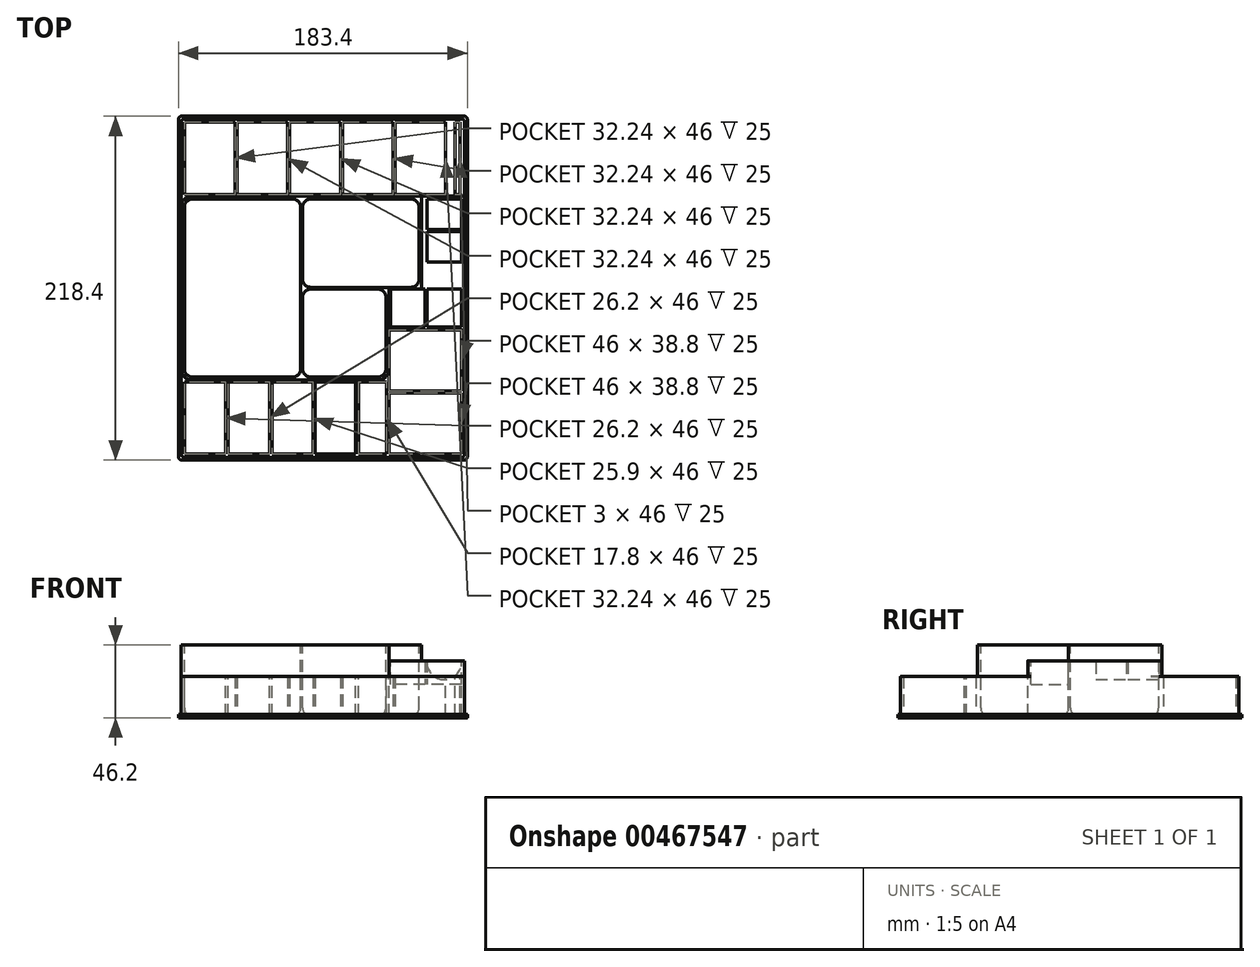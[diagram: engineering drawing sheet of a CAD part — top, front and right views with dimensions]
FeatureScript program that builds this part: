
annotation { "Feature Type Name" : "Feature", "Feature Type Description" : "" }
export const myFeature = defineFeature(function(context is Context, id is Id, definition is map)
    precondition{}
    {
        {
            var Q0;
            Q0=qCreatedBy(makeId("Top.planeOp"),FACE);
            var sketch = newSketch(context, id + "F0", { "sketchPlane" : qUnion([Q0])});
            skLineSegment(sketch, "E0.bottom", {"start": v(0, 0) * mm, "end": v(180, 0) * mm});
            skLineSegment(sketch, "E0.top", {"start": v(0, 215) * mm, "end": v(180, 215) * mm});
            skLineSegment(sketch, "E0.left", {"start": v(0, 0) * mm, "end": v(0, 215) * mm});
            skLineSegment(sketch, "E0.right", {"start": v(180, 0) * mm, "end": v(180, 215) * mm});
            skSolve(sketch);
        }
        {
            var Q0;
            Q0=qSketchRegion(id+"F0",true);
            extrude(context, id + "F1", {"entities" : qUnion([Q0]), "depth" : 25 * mm});
        }
        {
            var Q0;
            Q0=makeQuery(id+"F1.opExtrude","CAP_FACE",FACE,{"disambiguationData":[OSD([sQuery(id+"F0.wireOp",EDGE,"E0.bottom"),sQuery(id+"F0.wireOp",EDGE,"E0.top"),sQuery(id+"F0.wireOp",EDGE,"E0.left"),sQuery(id+"F0.wireOp",EDGE,"E0.right")])],"isStart":false});
            var sketch = newSketch(context, id + "F2", { "sketchPlane" : qUnion([Q0])});
            skLineSegment(sketch, "E1.bottom", {"start": v(2, 167) * mm, "end": v(2, 213) * mm});
            skLineSegment(sketch, "E1.top", {"start": v(168, 167) * mm, "end": v(168, 213) * mm});
            skLineSegment(sketch, "E1.left", {"start": v(2, 167) * mm, "end": v(168, 167) * mm});
            skLineSegment(sketch, "E1.right", {"start": v(2, 213) * mm, "end": v(168, 213) * mm});
            skLineSegment(sketch, "E2.bottom", {"start": v(110.8, 48) * mm, "end": v(57.8, 48) * mm});
            skLineSegment(sketch, "E2.top", {"start": v(110.8, 2) * mm, "end": v(57.8, 2) * mm});
            skLineSegment(sketch, "E2.left", {"start": v(110.8, 48) * mm, "end": v(110.8, 2) * mm});
            skLineSegment(sketch, "E2.right", {"start": v(57.8, 48) * mm, "end": v(57.8, 2) * mm});
            skLineSegment(sketch, "E3.bottom", {"start": v(2, 2) * mm, "end": v(28.2, 2) * mm});
            skLineSegment(sketch, "E3.top", {"start": v(2, 48) * mm, "end": v(28.2, 48) * mm});
            skLineSegment(sketch, "E3.left", {"start": v(2, 2) * mm, "end": v(2, 48) * mm});
            skLineSegment(sketch, "E3.right", {"start": v(28.2, 2) * mm, "end": v(28.2, 48) * mm});
            skLineSegment(sketch, "E4.bottom", {"start": v(132, 40.8) * mm, "end": v(178, 40.8) * mm});
            skLineSegment(sketch, "E4.top", {"start": v(132, 2) * mm, "end": v(178, 2) * mm});
            skLineSegment(sketch, "E4.left", {"start": v(132, 40.8) * mm, "end": v(132, 2) * mm});
            skLineSegment(sketch, "E4.right", {"start": v(178, 40.8) * mm, "end": v(178, 2) * mm});
            skLineSegment(sketch, "E5.bottom", {"start": v(132, 42) * mm, "end": v(178, 42) * mm});
            skLineSegment(sketch, "E5.top", {"start": v(132, 80.8) * mm, "end": v(178, 80.8) * mm});
            skLineSegment(sketch, "E5.left", {"start": v(132, 42) * mm, "end": v(132, 80.8) * mm});
            skLineSegment(sketch, "E5.right", {"start": v(178, 42) * mm, "end": v(178, 80.8) * mm});
            skLineSegment(sketch, "E6.bottom", {"start": v(29.9, 48) * mm, "end": v(56.1, 48) * mm});
            skLineSegment(sketch, "E6.top", {"start": v(29.9, 2) * mm, "end": v(56.1, 2) * mm});
            skLineSegment(sketch, "E6.left", {"start": v(29.9, 48) * mm, "end": v(29.9, 2) * mm});
            skLineSegment(sketch, "E6.right", {"start": v(56.1, 48) * mm, "end": v(56.1, 2) * mm});
            skLineSegment(sketch, "E7.bottom", {"start": v(130, 51) * mm, "end": v(77.1, 51) * mm});
            skLineSegment(sketch, "E7.top", {"start": v(130, 106.8) * mm, "end": v(77.1, 106.8) * mm});
            skLineSegment(sketch, "E7.right", {"start": v(77.1, 51) * mm, "end": v(77.1, 106.8) * mm});
            skLineSegment(sketch, "E8.top", {"start": v(178, 82.8) * mm, "end": v(178, 106.8) * mm});
            skLineSegment(sketch, "E8.left", {"start": v(133, 82.8) * mm, "end": v(178, 82.8) * mm});
            skLineSegment(sketch, "E8.right", {"start": v(133, 106.8) * mm, "end": v(178, 106.8) * mm});
            skLineSegment(sketch, "E9", {"start": v(2, 25) * mm, "end": v(0, 25) * mm, "construction": true});
            skLineSegment(sketch, "E10", {"start": v(28.2, 25) * mm, "end": v(29.9, 25) * mm, "construction": true});
            skLineSegment(sketch, "E11.bottom", {"start": v(156, 164) * mm, "end": v(178, 164) * mm});
            skLineSegment(sketch, "E11.top", {"start": v(156, 124) * mm, "end": v(178, 124) * mm});
            skLineSegment(sketch, "E11.left", {"start": v(156, 164) * mm, "end": v(156, 124) * mm});
            skLineSegment(sketch, "E11.right", {"start": v(178, 164) * mm, "end": v(178, 124) * mm});
            skLineSegment(sketch, "E12.bottom", {"start": v(151, 108) * mm, "end": v(77.1, 108) * mm});
            skLineSegment(sketch, "E12.top", {"start": v(151, 164) * mm, "end": v(77.1, 164) * mm});
            skLineSegment(sketch, "E12.left", {"start": v(151, 108) * mm, "end": v(151, 164) * mm});
            skLineSegment(sketch, "E12.right", {"start": v(77.1, 108) * mm, "end": v(77.1, 164) * mm});
            skLineSegment(sketch, "E13.bottom", {"start": v(2, 51) * mm, "end": v(75.9, 51) * mm});
            skLineSegment(sketch, "E13.top", {"start": v(2, 164) * mm, "end": v(75.9, 164) * mm});
            skLineSegment(sketch, "E13.left", {"start": v(2, 51) * mm, "end": v(2, 164) * mm});
            skLineSegment(sketch, "E13.right", {"start": v(75.9, 51) * mm, "end": v(75.9, 164) * mm});
            skLineSegment(sketch, "E14", {"start": v(133, 82.8) * mm, "end": v(133, 106.8) * mm});
            skLineSegment(sketch, "E15.bottom", {"start": v(130.3, 48) * mm, "end": v(130.3, 2) * mm});
            skLineSegment(sketch, "E15.top", {"start": v(112.5, 48) * mm, "end": v(112.5, 2) * mm});
            skLineSegment(sketch, "E15.left", {"start": v(130.3, 48) * mm, "end": v(112.5, 48) * mm});
            skLineSegment(sketch, "E15.right", {"start": v(130.3, 2) * mm, "end": v(112.5, 2) * mm});
            skLineSegment(sketch, "E16.bottom", {"start": v(174, 213) * mm, "end": v(177, 213) * mm});
            skLineSegment(sketch, "E16.top", {"start": v(174, 167) * mm, "end": v(177, 167) * mm});
            skLineSegment(sketch, "E16.left", {"start": v(174, 213) * mm, "end": v(174, 167) * mm});
            skLineSegment(sketch, "E16.right", {"start": v(177, 213) * mm, "end": v(177, 167) * mm});
            skLineSegment(sketch, "E17", {"start": v(56.1, 25) * mm, "end": v(57.8, 25) * mm, "construction": true});
            skLineSegment(sketch, "E18", {"start": v(110.8, 25) * mm, "end": v(112.5, 25) * mm, "construction": true});
            skLineSegment(sketch, "E19", {"start": v(130.3, 25) * mm, "end": v(132, 25) * mm, "construction": true});
            skLineSegment(sketch, "E20", {"start": v(130, 51) * mm, "end": v(130, 106.8) * mm});
            skSolve(sketch);
        }
        {
            var Q0;
            Q0=qSketchRegion(id+"F2",true);
            extrude(context, id + "F3", {"entities" : qUnion([Q0]), "operationType" : NewBodyOperationType.REMOVE, "endBound" : BoundingType.THROUGH_ALL, "oppositeDirection" : true, "depth" : 25 * mm});
        }
        {
            var Q0;
            Q0=qCreatedBy(makeId("Top.planeOp"),FACE);
            var sketch = newSketch(context, id + "F4", { "sketchPlane" : qUnion([Q0])});
            skLineSegment(sketch, "E21.0", {"start": v(0, 215) * mm, "end": v(180, 215) * mm});
            skLineSegment(sketch, "E21.1", {"start": v(0, 0) * mm, "end": v(0, 215) * mm});
            skLineSegment(sketch, "E21.2", {"start": v(0, 0) * mm, "end": v(180, 0) * mm});
            skLineSegment(sketch, "E21.3", {"start": v(180, 0) * mm, "end": v(180, 215) * mm});
            skSolve(sketch);
        }
        {
            var Q0;
            Q0=qSketchRegion(id+"F4",true);
            extrude(context, id + "F5", {"entities" : qUnion([Q0]), "operationType" : NewBodyOperationType.ADD, "oppositeDirection" : true, "depth" : 1.2 * mm});
        }
        {
            var Q0;
            Q0=qCreatedBy(makeId("Top.planeOp"),FACE);
            var sketch = newSketch(context, id + "F6", { "sketchPlane" : qUnion([Q0])});
            skLineSegment(sketch, "E22.bottom", {"start": v(34.24, 167) * mm, "end": v(34.24, 213) * mm});
            skLineSegment(sketch, "E22.top", {"start": v(35.44, 167) * mm, "end": v(35.44, 213) * mm});
            skLineSegment(sketch, "E22.left", {"start": v(34.24, 167) * mm, "end": v(35.44, 167) * mm});
            skLineSegment(sketch, "E22.right", {"start": v(34.24, 213) * mm, "end": v(35.44, 213) * mm});
            skLineSegment(sketch, "E23.0.1.0", {"start": v(67.68, 167) * mm, "end": v(67.68, 213) * mm});
            skLineSegment(sketch, "E23.0.1.1", {"start": v(68.88, 167) * mm, "end": v(68.88, 213) * mm});
            skLineSegment(sketch, "E23.0.1.2", {"start": v(67.68, 167) * mm, "end": v(68.88, 167) * mm});
            skLineSegment(sketch, "E23.0.1.3", {"start": v(67.68, 213) * mm, "end": v(68.88, 213) * mm});
            skLineSegment(sketch, "E23.0.2.0", {"start": v(101.12, 167) * mm, "end": v(101.12, 213) * mm});
            skLineSegment(sketch, "E23.0.2.1", {"start": v(102.32, 167) * mm, "end": v(102.32, 213) * mm});
            skLineSegment(sketch, "E23.0.2.2", {"start": v(101.12, 167) * mm, "end": v(102.32, 167) * mm});
            skLineSegment(sketch, "E23.0.2.3", {"start": v(101.12, 213) * mm, "end": v(102.32, 213) * mm});
            skLineSegment(sketch, "E23.direction1", {"start": v(35.44, 167) * mm, "end": v(35.44, 200.98) * mm, "construction": true});
            skLineSegment(sketch, "E23.direction2", {"start": v(35.44, 167) * mm, "end": v(68.88, 167) * mm, "construction": true});
            skLineSegment(sketch, "E24.0.0.3", {"start": v(134.56, 167) * mm, "end": v(134.56, 213) * mm});
            skLineSegment(sketch, "E24.3.0.3", {"start": v(135.76, 167) * mm, "end": v(135.76, 213) * mm});
            skLineSegment(sketch, "E24.6.0.3", {"start": v(134.56, 167) * mm, "end": v(135.76, 167) * mm});
            skLineSegment(sketch, "E24.9.0.3", {"start": v(134.56, 213) * mm, "end": v(135.76, 213) * mm});
            skLineSegment(sketch, "E25", {"start": v(34.24, 190) * mm, "end": v(2, 190) * mm, "construction": true});
            skPoint(sketch, "E25.endSnap0", {"position": v(34.24, 190) * mm});
            skLineSegment(sketch, "E26", {"start": v(135.76, 190) * mm, "end": v(168, 190) * mm, "construction": true});
            skLineSegment(sketch, "E27", {"start": v(35.44, 190) * mm, "end": v(67.68, 190) * mm, "construction": true});
            skLineSegment(sketch, "E28.bottom", {"start": v(83.7, 48) * mm, "end": v(84.9, 48) * mm});
            skLineSegment(sketch, "E28.top", {"start": v(83.7, 2) * mm, "end": v(84.9, 2) * mm});
            skLineSegment(sketch, "E28.left", {"start": v(83.7, 48) * mm, "end": v(83.7, 2) * mm});
            skLineSegment(sketch, "E28.right", {"start": v(84.9, 48) * mm, "end": v(84.9, 2) * mm});
            skLineSegment(sketch, "E29", {"start": v(83.7, 25) * mm, "end": v(57.8, 25) * mm, "construction": true});
            skLineSegment(sketch, "E30", {"start": v(84.9, 25) * mm, "end": v(110.8, 25) * mm, "construction": true});
            skLineSegment(sketch, "E31.bottom", {"start": v(156, 144.6) * mm, "end": v(178, 144.6) * mm});
            skLineSegment(sketch, "E31.top", {"start": v(156, 143.4) * mm, "end": v(178, 143.4) * mm});
            skLineSegment(sketch, "E31.left", {"start": v(156, 144.6) * mm, "end": v(156, 143.4) * mm});
            skLineSegment(sketch, "E31.right", {"start": v(178, 144.6) * mm, "end": v(178, 143.4) * mm});
            skLineSegment(sketch, "E32.bottom", {"start": v(156.1, 82.8) * mm, "end": v(156.1, 106.8) * mm});
            skLineSegment(sketch, "E32.top", {"start": v(154.9, 82.8) * mm, "end": v(154.9, 106.8) * mm});
            skLineSegment(sketch, "E32.left", {"start": v(154.9, 82.8) * mm, "end": v(156.1, 82.8) * mm});
            skLineSegment(sketch, "E32.right", {"start": v(154.9, 106.8) * mm, "end": v(156.1, 106.8) * mm});
            skSolve(sketch);
        }
        {
            var Q0;
            Q0=qSketchRegion(id+"F6",true);
            var Q1;
            Q1=makeQuery(id+"F1.opExtrude","CAP_FACE",FACE,{"disambiguationData":[OSD([sQuery(id+"F0.wireOp",EDGE,"E0.bottom"),sQuery(id+"F0.wireOp",EDGE,"E0.top"),sQuery(id+"F0.wireOp",EDGE,"E0.left"),sQuery(id+"F0.wireOp",EDGE,"E0.right")])],"isStart":false});
            extrude(context, id + "F7", {"entities" : qUnion([Q0]), "operationType" : NewBodyOperationType.ADD, "endBound" : BoundingType.UP_TO_SURFACE, "endBoundEntityFace" : qUnion([Q1]), "depth" : 25 * mm});
        }
        {
            var Q0;
            {var subQ0=sQuery(id+"F0.wireOp",EDGE,"E0.right");var subQ1=sQuery(id+"F0.wireOp",EDGE,"E0.left");var subQ2=sQuery(id+"F0.wireOp",EDGE,"E0.top");var subQ3=sQuery(id+"F0.wireOp",EDGE,"E0.bottom");Q0=makeQuery(id+"F7.boolean.opBoolean","MERGE",FACE,{"derivedFrom":[makeQuery(id+"F1.opExtrude","CAP_FACE",FACE,{"disambiguationData":[OSD([subQ3,subQ2,subQ1,subQ0])],"isStart":false}),makeQuery(id+"F7.opExtrude","CAP_FACE",FACE,{"disambiguationData":[OSD([subQ3,subQ2,subQ1,subQ0]),ownerDisambiguation([makeQuery(id+"F6.imprint","IMPRINT",EDGE,{"derivedFrom":sQuery(id+"F6.wireOp",EDGE,"E22.bottom")})])],"isStart":false}),makeQuery(id+"F7.opExtrude","CAP_FACE",FACE,{"disambiguationData":[OSD([subQ3,subQ2,subQ1,subQ0]),ownerDisambiguation([makeQuery(id+"F6.imprint","IMPRINT",EDGE,{"derivedFrom":sQuery(id+"F6.wireOp",EDGE,"E23.0.1.0")})])],"isStart":false}),makeQuery(id+"F7.opExtrude","CAP_FACE",FACE,{"disambiguationData":[OSD([subQ3,subQ2,subQ1,subQ0]),ownerDisambiguation([makeQuery(id+"F6.imprint","IMPRINT",EDGE,{"derivedFrom":sQuery(id+"F6.wireOp",EDGE,"E23.0.2.0")})])],"isStart":false}),makeQuery(id+"F7.opExtrude","CAP_FACE",FACE,{"disambiguationData":[OSD([subQ3,subQ2,subQ1,subQ0]),ownerDisambiguation([makeQuery(id+"F6.imprint","IMPRINT",EDGE,{"derivedFrom":sQuery(id+"F6.wireOp",EDGE,"E24.0.0.3")})])],"isStart":false}),makeQuery(id+"F7.opExtrude","CAP_FACE",FACE,{"disambiguationData":[OSD([subQ3,subQ2,subQ1,subQ0]),ownerDisambiguation([makeQuery(id+"F6.imprint","IMPRINT",EDGE,{"derivedFrom":sQuery(id+"F6.wireOp",EDGE,"E28.bottom")})])],"isStart":false}),makeQuery(id+"F7.opExtrude","CAP_FACE",FACE,{"disambiguationData":[OSD([subQ3,subQ2,subQ1,subQ0]),ownerDisambiguation([makeQuery(id+"F6.imprint","IMPRINT",EDGE,{"derivedFrom":sQuery(id+"F6.wireOp",EDGE,"E31.bottom")})])],"isStart":false}),makeQuery(id+"F7.opExtrude","CAP_FACE",FACE,{"disambiguationData":[OSD([subQ3,subQ2,subQ1,subQ0]),ownerDisambiguation([makeQuery(id+"F6.imprint","IMPRINT",EDGE,{"derivedFrom":sQuery(id+"F6.wireOp",EDGE,"E32.bottom")})])],"isStart":false})]});}
            var sketch = newSketch(context, id + "F8", { "sketchPlane" : qUnion([Q0])});
            skLineSegment(sketch, "E33.0", {"start": v(156.1, 82.8) * mm, "end": v(178, 82.8) * mm});
            skLineSegment(sketch, "E34.0", {"start": v(156.1, 82.8) * mm, "end": v(156.1, 106.8) * mm});
            skLineSegment(sketch, "E35.0", {"start": v(156.1, 106.8) * mm, "end": v(178, 106.8) * mm});
            skLineSegment(sketch, "E36.0", {"start": v(178, 82.8) * mm, "end": v(178, 106.8) * mm});
            skLineSegment(sketch, "E36.1", {"start": v(154.9, 82.8) * mm, "end": v(154.9, 106.8) * mm});
            skLineSegment(sketch, "E36.2", {"start": v(133, 82.8) * mm, "end": v(154.9, 82.8) * mm});
            skLineSegment(sketch, "E36.3", {"start": v(133, 82.8) * mm, "end": v(133, 106.8) * mm});
            skLineSegment(sketch, "E36.4", {"start": v(133, 106.8) * mm, "end": v(154.9, 106.8) * mm});
            skLineSegment(sketch, "E37.0", {"start": v(156, 124) * mm, "end": v(178, 124) * mm});
            skLineSegment(sketch, "E37.1", {"start": v(156, 143.4) * mm, "end": v(156, 124) * mm});
            skLineSegment(sketch, "E37.2", {"start": v(156, 143.4) * mm, "end": v(178, 143.4) * mm});
            skLineSegment(sketch, "E37.3", {"start": v(178, 143.4) * mm, "end": v(178, 124) * mm});
            skLineSegment(sketch, "E37.4", {"start": v(178, 164) * mm, "end": v(178, 144.6) * mm});
            skLineSegment(sketch, "E37.5", {"start": v(156, 144.6) * mm, "end": v(178, 144.6) * mm});
            skLineSegment(sketch, "E37.6", {"start": v(156, 164) * mm, "end": v(156, 144.6) * mm});
            skLineSegment(sketch, "E37.7", {"start": v(156, 164) * mm, "end": v(178, 164) * mm});
            skLineSegment(sketch, "E38.0", {"start": v(2, 51) * mm, "end": v(75.9, 51) * mm});
            skLineSegment(sketch, "E38.1", {"start": v(2, 51) * mm, "end": v(2, 164) * mm});
            skLineSegment(sketch, "E38.2", {"start": v(2, 164) * mm, "end": v(75.9, 164) * mm});
            skLineSegment(sketch, "E38.3", {"start": v(75.9, 51) * mm, "end": v(75.9, 164) * mm});
            skLineSegment(sketch, "E39.0", {"start": v(130, 51) * mm, "end": v(77.1, 51) * mm});
            skLineSegment(sketch, "E39.1", {"start": v(77.1, 51) * mm, "end": v(77.1, 106.8) * mm});
            skLineSegment(sketch, "E39.2", {"start": v(151, 108) * mm, "end": v(77.1, 108) * mm});
            skLineSegment(sketch, "E39.3", {"start": v(130, 106.8) * mm, "end": v(77.1, 106.8) * mm});
            skLineSegment(sketch, "E39.4", {"start": v(77.1, 108) * mm, "end": v(77.1, 164) * mm});
            skLineSegment(sketch, "E39.7", {"start": v(151, 164) * mm, "end": v(77.1, 164) * mm});
            skLineSegment(sketch, "E40.0", {"start": v(151, 108) * mm, "end": v(151, 164) * mm});
            skLineSegment(sketch, "E40.1", {"start": v(130, 51) * mm, "end": v(130, 106.8) * mm});
            skLineSegment(sketch, "E41", {"start": v(0, 49) * mm, "end": v(132, 49) * mm});
            skLineSegment(sketch, "E42", {"start": v(132, 49) * mm, "end": v(132, 80.8) * mm});
            skLineSegment(sketch, "E43", {"start": v(132, 80.8) * mm, "end": v(180, 80.8) * mm});
            skLineSegment(sketch, "E44", {"start": v(180, 80.8) * mm, "end": v(180, 166) * mm});
            skLineSegment(sketch, "E45", {"start": v(180, 166) * mm, "end": v(132, 166) * mm});
            skLineSegment(sketch, "E46", {"start": v(132, 166) * mm, "end": v(132, 166) * mm});
            skLineSegment(sketch, "E47", {"start": v(132, 166) * mm, "end": v(0, 166) * mm});
            skLineSegment(sketch, "E48", {"start": v(0, 166) * mm, "end": v(0, 49) * mm});
            skLineSegment(sketch, "E49", {"start": v(2, 51) * mm, "end": v(2, 49) * mm, "construction": true});
            skLineSegment(sketch, "E50", {"start": v(2, 164) * mm, "end": v(2, 166) * mm, "construction": true});
            skLineSegment(sketch, "E51", {"start": v(130, 51) * mm, "end": v(132, 51) * mm, "construction": true});
            skLineSegment(sketch, "E52", {"start": v(130, 51) * mm, "end": v(130, 49) * mm, "construction": true});
            skLineSegment(sketch, "E53", {"start": v(167, 164) * mm, "end": v(167, 166) * mm, "construction": true});
            skLineSegment(sketch, "E54", {"start": v(2, 51) * mm, "end": v(0, 51) * mm, "construction": true});
            skSolve(sketch);
        }
        {
            var Q0;
            Q0 = qSketchRegion(id + "F8", true);
            extrude(context, id + "F9", {"entities" : qUnion([Q0]), "operationType" : NewBodyOperationType.ADD, "depth" : 20 * mm});
        }
        {
            var Q0;
            Q0=makeQuery(id+"F3.boolean.opBoolean","COPY",FACE,{"derivedFrom":makeQuery(id+"F3.opExtrude","SWEPT_FACE",FACE,{"disambiguationData":[OSD([sQuery(id+"F2.wireOp",EDGE,"E14")])]})});
            var sketch = newSketch(context, id + "F10", { "sketchPlane" : qUnion([Q0])});
            skLineSegment(sketch, "E55.0", {"start": v(106.8, 0) * mm, "end": v(106.8, 20) * mm});
            skLineSegment(sketch, "E55.1", {"start": v(82.8, 0) * mm, "end": v(82.8, 20) * mm});
            skLineSegment(sketch, "E55.2", {"start": v(82.8, 0) * mm, "end": v(106.8, 0) * mm});
            skLineSegment(sketch, "E56", {"start": v(82.8, 20) * mm, "end": v(106.8, 20) * mm});
            skSolve(sketch);
        }
        {
            var Q0;
            Q0=qSketchRegion(id+"F10",true);
            var Q1;
            Q1=makeQuery(id+"F3.boolean.opBoolean","COPY",FACE,{"derivedFrom":makeQuery(id+"F3.opExtrude","SWEPT_FACE",FACE,{"disambiguationData":[OSD([sQuery(id+"F2.wireOp",EDGE,"E8.top")])]})});
            extrude(context, id + "F11", {"entities" : qUnion([Q0]), "operationType" : NewBodyOperationType.ADD, "endBound" : BoundingType.UP_TO_SURFACE, "endBoundEntityFace" : qUnion([Q1]), "depth" : 25 * mm});
        }
        {
            var Q0;
            Q0=makeQuery(id+"F3.boolean.opBoolean","COPY",FACE,{"derivedFrom":makeQuery(id+"F3.opExtrude","SWEPT_FACE",FACE,{"disambiguationData":[OSD([sQuery(id+"F2.wireOp",EDGE,"E11.bottom")])]})});
            var sketch = newSketch(context, id + "F12", { "sketchPlane" : qUnion([Q0])});
            skLineSegment(sketch, "E57.0", {"start": v(156, 0) * mm, "end": v(156, 34) * mm});
            skLineSegment(sketch, "E57.1", {"start": v(178, 0) * mm, "end": v(178, 34) * mm});
            skLineSegment(sketch, "E57.2", {"start": v(156, 0) * mm, "end": v(178, 0) * mm});
            skArc(sketch, "E58", {"start": v(156, 34) * mm, "mid": v(167, 23) * mm, "end": v(178, 34) * mm});
            skSolve(sketch);
        }
        {
            var Q0;
            Q0=qSketchRegion(id+"F12",true);
            var Q1;
            Q1=makeQuery(id+"F3.boolean.opBoolean","COPY",FACE,{"derivedFrom":makeQuery(id+"F3.opExtrude","SWEPT_FACE",FACE,{"disambiguationData":[OSD([sQuery(id+"F2.wireOp",EDGE,"E11.top")])]})});
            extrude(context, id + "F13", {"entities" : qUnion([Q0]), "operationType" : NewBodyOperationType.ADD, "endBound" : BoundingType.UP_TO_SURFACE, "endBoundEntityFace" : qUnion([Q1]), "depth" : 25 * mm});
        }
        {
            var Q0;
            Q0=makeQuery(id+"F5.opExtrude","CAP_FACE",FACE,{"disambiguationData":[OSD([sQuery(id+"F4.wireOp",EDGE,"E21.0"),sQuery(id+"F4.wireOp",EDGE,"E21.1"),sQuery(id+"F4.wireOp",EDGE,"E21.2"),sQuery(id+"F4.wireOp",EDGE,"E21.3")])],"isStart":false});
            var sketch = newSketch(context, id + "F14", { "sketchPlane" : qUnion([Q0])});
            skLineSegment(sketch, "E59", {"start": v(0, 0) * mm, "end": v(180, 0) * mm});
            skLineSegment(sketch, "E60", {"start": v(0, 0) * mm, "end": v(0, -215) * mm});
            skLineSegment(sketch, "E61", {"start": v(0, -215) * mm, "end": v(180, -215) * mm});
            skLineSegment(sketch, "E62", {"start": v(180, 0) * mm, "end": v(180, -215) * mm});
            skLineSegment(sketch, "E63.0", {"start": v(181.7, 1.7) * mm, "end": v(181.7, -216.7) * mm});
            skLineSegment(sketch, "E63.1", {"start": v(-1.7, 1.7) * mm, "end": v(181.7, 1.7) * mm});
            skLineSegment(sketch, "E63.2", {"start": v(-1.7, 1.7) * mm, "end": v(-1.7, -216.7) * mm});
            skLineSegment(sketch, "E63.3", {"start": v(-1.7, -216.7) * mm, "end": v(181.7, -216.7) * mm});
            skSolve(sketch);
        }
        {
            var Q0;
            Q0=qSketchRegion(id+"F14",true);
            extrude(context, id + "F15", {"entities" : qUnion([Q0]), "operationType" : NewBodyOperationType.ADD, "oppositeDirection" : true, "depth" : 2 * mm});
        }
        {
            var Q0;
            Q0=makeQuery(id+"F9.opExtrude","CAP_FACE",FACE,{"disambiguationData":[OSD([sQuery(id+"F8.wireOp",EDGE,"E33.0"),sQuery(id+"F8.wireOp",EDGE,"E34.0"),sQuery(id+"F8.wireOp",EDGE,"E35.0"),sQuery(id+"F8.wireOp",EDGE,"E36.0"),sQuery(id+"F8.wireOp",EDGE,"E36.1"),sQuery(id+"F8.wireOp",EDGE,"E36.2"),sQuery(id+"F8.wireOp",EDGE,"E36.3"),sQuery(id+"F8.wireOp",EDGE,"E36.4"),sQuery(id+"F8.wireOp",EDGE,"E37.0"),sQuery(id+"F8.wireOp",EDGE,"E37.1"),sQuery(id+"F8.wireOp",EDGE,"E37.2"),sQuery(id+"F8.wireOp",EDGE,"E37.3"),sQuery(id+"F8.wireOp",EDGE,"E37.4"),sQuery(id+"F8.wireOp",EDGE,"E37.5"),sQuery(id+"F8.wireOp",EDGE,"E37.6"),sQuery(id+"F8.wireOp",EDGE,"E37.7"),sQuery(id+"F8.wireOp",EDGE,"E38.0"),sQuery(id+"F8.wireOp",EDGE,"E38.1"),sQuery(id+"F8.wireOp",EDGE,"E38.2"),sQuery(id+"F8.wireOp",EDGE,"E38.3"),sQuery(id+"F8.wireOp",EDGE,"E39.0"),sQuery(id+"F8.wireOp",EDGE,"E39.1"),sQuery(id+"F8.wireOp",EDGE,"E39.2"),sQuery(id+"F8.wireOp",EDGE,"E39.3"),sQuery(id+"F8.wireOp",EDGE,"E39.4"),sQuery(id+"F8.wireOp",EDGE,"E39.5"),sQuery(id+"F8.wireOp",EDGE,"E39.6"),sQuery(id+"F8.wireOp",EDGE,"E39.7"),sQuery(id+"F8.wireOp",EDGE,"E40.0"),sQuery(id+"F8.wireOp",EDGE,"E40.1"),sQuery(id+"F8.wireOp",EDGE,"E41"),sQuery(id+"F8.wireOp",EDGE,"XPu77cuN-X5yf-Tfu9-wkux-P44unaFSe9BC"),sQuery(id+"F8.wireOp",EDGE,"gCxIZk9a-GLua-Ydf3-ZZly-w7nDAVDTeZa5"),sQuery(id+"F8.wireOp",EDGE,"E42"),sQuery(id+"F8.wireOp",EDGE,"E43"),sQuery(id+"F8.wireOp",EDGE,"E44"),sQuery(id+"F8.wireOp",EDGE,"E45"),sQuery(id+"F8.wireOp",EDGE,"E46"),sQuery(id+"F8.wireOp",EDGE,"E47"),sQuery(id+"F8.wireOp",EDGE,"E48")])],"isStart":false});
            var sketch = newSketch(context, id + "F16", { "sketchPlane" : qUnion([Q0])});
            skLineSegment(sketch, "E64.0", {"start": v(132, 80.8) * mm, "end": v(180, 80.8) * mm});
            skLineSegment(sketch, "E64.1", {"start": v(180, 80.8) * mm, "end": v(180, 166) * mm});
            skLineSegment(sketch, "E64.2", {"start": v(180, 166) * mm, "end": v(152.5, 166) * mm});
            skLineSegment(sketch, "E65", {"start": v(132, 80.8) * mm, "end": v(132, 106.8) * mm});
            skLineSegment(sketch, "E66", {"start": v(132, 106.8) * mm, "end": v(152.5, 106.8) * mm});
            skLineSegment(sketch, "E67", {"start": v(152.5, 106.8) * mm, "end": v(152.5, 166) * mm});
            skSolve(sketch);
        }
        {
            var Q0;
            Q0 = qSketchRegion(id + "F16", true);
            extrude(context, id + "F17", {"entities" : qUnion([Q0]), "operationType" : NewBodyOperationType.REMOVE, "oppositeDirection" : true, "depth" : 10 * mm});
        }
        {
            var Q0;
            Q0=makeQuery(id+"F5.boolean.opBoolean","MERGE",EDGE,{"derivedFrom":[makeQuery(id+"F1.opExtrude","SWEPT_EDGE",EDGE,{"disambiguationData":[OSD([sQuery(id+"F0.wireOp",EDGE,"E0.bottom"),sQuery(id+"F0.wireOp",EDGE,"E0.right")])]}),makeQuery(id+"F5.opExtrude","SWEPT_EDGE",EDGE,{"disambiguationData":[OSD([sQuery(id+"F4.wireOp",EDGE,"E21.2"),sQuery(id+"F4.wireOp",EDGE,"E21.3")])]})]});
            var Q1;
            Q1=makeQuery(id+"F9.opExtrude","SWEPT_EDGE",EDGE,{"disambiguationData":[OSD([sQuery(id+"F0.wireOp",EDGE,"E0.right"),sQuery(id+"F8.wireOp",EDGE,"E43"),sQuery(id+"F8.wireOp",EDGE,"E44")])]});
            var Q2;
            Q2=makeQuery(id+"F9.opExtrude","SWEPT_EDGE",EDGE,{"disambiguationData":[OSD([sQuery(id+"F0.wireOp",EDGE,"E0.right"),sQuery(id+"F8.wireOp",EDGE,"E44"),sQuery(id+"F8.wireOp",EDGE,"E45")])]});
            var Q3;
            Q3=makeQuery(id+"F5.boolean.opBoolean","MERGE",EDGE,{"derivedFrom":[makeQuery(id+"F1.opExtrude","SWEPT_EDGE",EDGE,{"disambiguationData":[OSD([sQuery(id+"F0.wireOp",EDGE,"E0.top"),sQuery(id+"F0.wireOp",EDGE,"E0.right")])]}),makeQuery(id+"F5.opExtrude","SWEPT_EDGE",EDGE,{"disambiguationData":[OSD([sQuery(id+"F4.wireOp",EDGE,"E21.0"),sQuery(id+"F4.wireOp",EDGE,"E21.3")])]})]});
            var Q4;
            Q4=makeQuery(id+"F5.boolean.opBoolean","MERGE",EDGE,{"derivedFrom":[makeQuery(id+"F1.opExtrude","SWEPT_EDGE",EDGE,{"disambiguationData":[OSD([sQuery(id+"F0.wireOp",EDGE,"E0.top"),sQuery(id+"F0.wireOp",EDGE,"E0.left")])]}),makeQuery(id+"F5.opExtrude","SWEPT_EDGE",EDGE,{"disambiguationData":[OSD([sQuery(id+"F4.wireOp",EDGE,"E21.0"),sQuery(id+"F4.wireOp",EDGE,"E21.1")])]})]});
            var Q5;
            Q5=makeQuery(id+"F5.boolean.opBoolean","MERGE",EDGE,{"derivedFrom":[makeQuery(id+"F1.opExtrude","SWEPT_EDGE",EDGE,{"disambiguationData":[OSD([sQuery(id+"F0.wireOp",EDGE,"E0.bottom"),sQuery(id+"F0.wireOp",EDGE,"E0.left")])]}),makeQuery(id+"F5.opExtrude","SWEPT_EDGE",EDGE,{"disambiguationData":[OSD([sQuery(id+"F4.wireOp",EDGE,"E21.1"),sQuery(id+"F4.wireOp",EDGE,"E21.2")])]})]});
            var Q6;
            Q6=makeQuery(id+"F15.opExtrude","SWEPT_EDGE",EDGE,{"disambiguationData":[OSD([sQuery(id+"F14.wireOp",EDGE,"E63.1"),sQuery(id+"F14.wireOp",EDGE,"E63.2")])]});
            var Q7;
            Q7=makeQuery(id+"F15.opExtrude","SWEPT_EDGE",EDGE,{"disambiguationData":[OSD([sQuery(id+"F14.wireOp",EDGE,"E63.0"),sQuery(id+"F14.wireOp",EDGE,"E63.1")])]});
            var Q8;
            Q8=makeQuery(id+"F15.opExtrude","SWEPT_EDGE",EDGE,{"disambiguationData":[OSD([sQuery(id+"F14.wireOp",EDGE,"E63.0"),sQuery(id+"F14.wireOp",EDGE,"E63.3")])]});
            var Q9;
            Q9=makeQuery(id+"F15.opExtrude","SWEPT_EDGE",EDGE,{"disambiguationData":[OSD([sQuery(id+"F14.wireOp",EDGE,"E63.2"),sQuery(id+"F14.wireOp",EDGE,"E63.3")])]});
            fillet(context, id + "F18", {"entities" : qUnion([Q0, Q1, Q2, Q3, Q4, Q5, Q6, Q7, Q8, Q9]), "radius" : 2 * mm, "tangentPropagation" : true, "allowEdgeOverflow" : false});
        }
        {
            var Q0;
            Q0=makeQuery(id+"F5.boolean.opBoolean","SPLIT",FACE,{"disambiguationData":[TD([makeQuery(id+"F3.boolean.opBoolean","COPY",FACE,{"derivedFrom":makeQuery(id+"F3.opExtrude","SWEPT_FACE",FACE,{"disambiguationData":[OSD([sQuery(id+"F2.wireOp",EDGE,"E7.bottom")])]})})])],"derivedFrom":makeQuery(id+"F5.opExtrude","CAP_FACE",FACE,{"disambiguationData":[OSD([sQuery(id+"F4.wireOp",EDGE,"E21.0"),sQuery(id+"F4.wireOp",EDGE,"E21.1"),sQuery(id+"F4.wireOp",EDGE,"E21.2"),sQuery(id+"F4.wireOp",EDGE,"E21.3")])],"isStart":true})});
            var Q1;
            Q1=makeQuery(id+"F5.boolean.opBoolean","SPLIT",FACE,{"disambiguationData":[TD([makeQuery(id+"F3.boolean.opBoolean","COPY",FACE,{"derivedFrom":makeQuery(id+"F3.opExtrude","SWEPT_FACE",FACE,{"disambiguationData":[OSD([sQuery(id+"F2.wireOp",EDGE,"E12.bottom")])]})})])],"derivedFrom":makeQuery(id+"F5.opExtrude","CAP_FACE",FACE,{"disambiguationData":[OSD([sQuery(id+"F4.wireOp",EDGE,"E21.0"),sQuery(id+"F4.wireOp",EDGE,"E21.1"),sQuery(id+"F4.wireOp",EDGE,"E21.2"),sQuery(id+"F4.wireOp",EDGE,"E21.3")])],"isStart":true})});
            var Q2;
            Q2=makeQuery(id+"F5.boolean.opBoolean","SPLIT",FACE,{"disambiguationData":[TD([makeQuery(id+"F3.boolean.opBoolean","COPY",FACE,{"derivedFrom":makeQuery(id+"F3.opExtrude","SWEPT_FACE",FACE,{"disambiguationData":[OSD([sQuery(id+"F2.wireOp",EDGE,"E13.bottom")])]})})])],"derivedFrom":makeQuery(id+"F5.opExtrude","CAP_FACE",FACE,{"disambiguationData":[OSD([sQuery(id+"F4.wireOp",EDGE,"E21.0"),sQuery(id+"F4.wireOp",EDGE,"E21.1"),sQuery(id+"F4.wireOp",EDGE,"E21.2"),sQuery(id+"F4.wireOp",EDGE,"E21.3")])],"isStart":true})});
            var Q3;
            Q3=makeQuery(id+"F9.boolean.opBoolean","MERGE",EDGE,{"derivedFrom":[makeQuery(id+"F3.boolean.opBoolean","COPY",EDGE,{"derivedFrom":makeQuery(id+"F3.opExtrude","SWEPT_EDGE",EDGE,{"disambiguationData":[OSD([sQuery(id+"F2.wireOp",EDGE,"E13.bottom"),sQuery(id+"F2.wireOp",EDGE,"E13.left")])]})}),makeQuery(id+"F9.opExtrude","SWEPT_EDGE",EDGE,{"disambiguationData":[OSD([sQuery(id+"F8.wireOp",EDGE,"E38.0"),sQuery(id+"F8.wireOp",EDGE,"E38.1")])]})]});
            var Q4;
            Q4=makeQuery(id+"F9.boolean.opBoolean","MERGE",EDGE,{"derivedFrom":[makeQuery(id+"F3.boolean.opBoolean","COPY",EDGE,{"derivedFrom":makeQuery(id+"F3.opExtrude","SWEPT_EDGE",EDGE,{"disambiguationData":[OSD([sQuery(id+"F2.wireOp",EDGE,"E13.top"),sQuery(id+"F2.wireOp",EDGE,"E13.left")])]})}),makeQuery(id+"F9.opExtrude","SWEPT_EDGE",EDGE,{"disambiguationData":[OSD([sQuery(id+"F8.wireOp",EDGE,"E38.1"),sQuery(id+"F8.wireOp",EDGE,"E38.2")])]})]});
            var Q5;
            Q5=makeQuery(id+"F9.boolean.opBoolean","MERGE",EDGE,{"derivedFrom":[makeQuery(id+"F3.boolean.opBoolean","COPY",EDGE,{"derivedFrom":makeQuery(id+"F3.opExtrude","SWEPT_EDGE",EDGE,{"disambiguationData":[OSD([sQuery(id+"F2.wireOp",EDGE,"E13.top"),sQuery(id+"F2.wireOp",EDGE,"E13.right")])]})}),makeQuery(id+"F9.opExtrude","SWEPT_EDGE",EDGE,{"disambiguationData":[OSD([sQuery(id+"F8.wireOp",EDGE,"E38.2"),sQuery(id+"F8.wireOp",EDGE,"E38.3")])]})]});
            var Q6;
            Q6=makeQuery(id+"F9.boolean.opBoolean","MERGE",EDGE,{"derivedFrom":[makeQuery(id+"F3.boolean.opBoolean","COPY",EDGE,{"derivedFrom":makeQuery(id+"F3.opExtrude","SWEPT_EDGE",EDGE,{"disambiguationData":[OSD([sQuery(id+"F2.wireOp",EDGE,"E13.bottom"),sQuery(id+"F2.wireOp",EDGE,"E13.right")])]})}),makeQuery(id+"F9.opExtrude","SWEPT_EDGE",EDGE,{"disambiguationData":[OSD([sQuery(id+"F8.wireOp",EDGE,"E38.0"),sQuery(id+"F8.wireOp",EDGE,"E38.3")])]})]});
            var Q7;
            Q7=makeQuery(id+"F9.boolean.opBoolean","MERGE",EDGE,{"derivedFrom":[makeQuery(id+"F3.boolean.opBoolean","COPY",EDGE,{"derivedFrom":makeQuery(id+"F3.opExtrude","SWEPT_EDGE",EDGE,{"disambiguationData":[OSD([sQuery(id+"F2.wireOp",EDGE,"E7.top"),sQuery(id+"F2.wireOp",EDGE,"E7.right")])]})}),makeQuery(id+"F9.opExtrude","SWEPT_EDGE",EDGE,{"disambiguationData":[OSD([sQuery(id+"F8.wireOp",EDGE,"E39.1"),sQuery(id+"F8.wireOp",EDGE,"E39.3")])]})]});
            var Q8;
            Q8=makeQuery(id+"F9.boolean.opBoolean","MERGE",EDGE,{"derivedFrom":[makeQuery(id+"F3.boolean.opBoolean","COPY",EDGE,{"derivedFrom":makeQuery(id+"F3.opExtrude","SWEPT_EDGE",EDGE,{"disambiguationData":[OSD([sQuery(id+"F2.wireOp",EDGE,"E12.top"),sQuery(id+"F2.wireOp",EDGE,"E12.right")])]})}),makeQuery(id+"F9.opExtrude","SWEPT_EDGE",EDGE,{"disambiguationData":[OSD([sQuery(id+"F8.wireOp",EDGE,"E39.4"),sQuery(id+"F8.wireOp",EDGE,"E39.7")])]})]});
            var Q9;
            Q9=makeQuery(id+"F9.boolean.opBoolean","MERGE",EDGE,{"derivedFrom":[makeQuery(id+"F3.boolean.opBoolean","COPY",EDGE,{"derivedFrom":makeQuery(id+"F3.opExtrude","SWEPT_EDGE",EDGE,{"disambiguationData":[OSD([sQuery(id+"F2.wireOp",EDGE,"E12.top"),sQuery(id+"F2.wireOp",EDGE,"E12.left")])]})}),makeQuery(id+"F9.opExtrude","SWEPT_EDGE",EDGE,{"disambiguationData":[OSD([sQuery(id+"F8.wireOp",EDGE,"E39.7"),sQuery(id+"F8.wireOp",EDGE,"E40.0")])]})]});
            var Q10;
            Q10=makeQuery(id+"F9.boolean.opBoolean","MERGE",EDGE,{"derivedFrom":[makeQuery(id+"F3.boolean.opBoolean","COPY",EDGE,{"derivedFrom":makeQuery(id+"F3.opExtrude","SWEPT_EDGE",EDGE,{"disambiguationData":[OSD([sQuery(id+"F2.wireOp",EDGE,"E12.bottom"),sQuery(id+"F2.wireOp",EDGE,"E12.left")])]})}),makeQuery(id+"F9.opExtrude","SWEPT_EDGE",EDGE,{"disambiguationData":[OSD([sQuery(id+"F8.wireOp",EDGE,"E39.2"),sQuery(id+"F8.wireOp",EDGE,"E40.0")])]})]});
            var Q11;
            Q11=makeQuery(id+"F9.boolean.opBoolean","MERGE",EDGE,{"derivedFrom":[makeQuery(id+"F3.boolean.opBoolean","COPY",EDGE,{"derivedFrom":makeQuery(id+"F3.opExtrude","SWEPT_EDGE",EDGE,{"disambiguationData":[OSD([sQuery(id+"F2.wireOp",EDGE,"E7.top"),sQuery(id+"F2.wireOp",EDGE,"E20")])]})}),makeQuery(id+"F9.opExtrude","SWEPT_EDGE",EDGE,{"disambiguationData":[OSD([sQuery(id+"F8.wireOp",EDGE,"E39.3"),sQuery(id+"F8.wireOp",EDGE,"E40.1")])]})]});
            var Q12;
            Q12=makeQuery(id+"F9.boolean.opBoolean","MERGE",EDGE,{"derivedFrom":[makeQuery(id+"F3.boolean.opBoolean","COPY",EDGE,{"derivedFrom":makeQuery(id+"F3.opExtrude","SWEPT_EDGE",EDGE,{"disambiguationData":[OSD([sQuery(id+"F2.wireOp",EDGE,"E7.bottom"),sQuery(id+"F2.wireOp",EDGE,"E20")])]})}),makeQuery(id+"F9.opExtrude","SWEPT_EDGE",EDGE,{"disambiguationData":[OSD([sQuery(id+"F8.wireOp",EDGE,"E39.0"),sQuery(id+"F8.wireOp",EDGE,"E40.1")])]})]});
            var Q13;
            Q13=makeQuery(id+"F9.boolean.opBoolean","MERGE",EDGE,{"derivedFrom":[makeQuery(id+"F3.boolean.opBoolean","COPY",EDGE,{"derivedFrom":makeQuery(id+"F3.opExtrude","SWEPT_EDGE",EDGE,{"disambiguationData":[OSD([sQuery(id+"F2.wireOp",EDGE,"E7.bottom"),sQuery(id+"F2.wireOp",EDGE,"E7.right")])]})}),makeQuery(id+"F9.opExtrude","SWEPT_EDGE",EDGE,{"disambiguationData":[OSD([sQuery(id+"F8.wireOp",EDGE,"E39.0"),sQuery(id+"F8.wireOp",EDGE,"E39.1")])]})]});
            var Q14;
            Q14=makeQuery(id+"F9.boolean.opBoolean","MERGE",EDGE,{"derivedFrom":[makeQuery(id+"F3.boolean.opBoolean","COPY",EDGE,{"derivedFrom":makeQuery(id+"F3.opExtrude","SWEPT_EDGE",EDGE,{"disambiguationData":[OSD([sQuery(id+"F2.wireOp",EDGE,"E12.bottom"),sQuery(id+"F2.wireOp",EDGE,"E12.right")])]})}),makeQuery(id+"F9.opExtrude","SWEPT_EDGE",EDGE,{"disambiguationData":[OSD([sQuery(id+"F8.wireOp",EDGE,"E39.2"),sQuery(id+"F8.wireOp",EDGE,"E39.4")])]})]});
            fillet(context, id + "F19", {"entities" : qUnion([Q0, Q1, Q2, Q3, Q4, Q5, Q6, Q7, Q8, Q9, Q10, Q11, Q12, Q13, Q14]), "radius" : 5 * mm, "tangentPropagation" : true, "allowEdgeOverflow" : false});
        }
        {
            var Q0;
            Q0=makeQuery(id+"F9.opExtrude","SWEPT_EDGE",EDGE,{"disambiguationData":[OSD([sQuery(id+"F8.wireOp",EDGE,"E41"),sQuery(id+"F8.wireOp",EDGE,"E42")])]});
            var Q1;
            Q1=makeQuery(id+"F9.opExtrude","SWEPT_EDGE",EDGE,{"disambiguationData":[OSD([sQuery(id+"F0.wireOp",EDGE,"E0.left"),sQuery(id+"F8.wireOp",EDGE,"E41"),sQuery(id+"F8.wireOp",EDGE,"E48")])]});
            var Q2;
            Q2=makeQuery(id+"F17.boolean.opBoolean","COPY",EDGE,{"derivedFrom":makeQuery(id+"F17.opExtrude","SWEPT_EDGE",EDGE,{"disambiguationData":[OSD([sQuery(id+"F8.wireOp",EDGE,"E36.4"),sQuery(id+"F16.wireOp",EDGE,"E66"),sQuery(id+"F16.wireOp",EDGE,"E67")])]})});
            var Q3;
            Q3=makeQuery(id+"F17.boolean.opBoolean","COPY",EDGE,{"derivedFrom":makeQuery(id+"F17.opExtrude","SWEPT_EDGE",EDGE,{"disambiguationData":[OSD([sQuery(id+"F8.wireOp",EDGE,"E45"),sQuery(id+"F8.wireOp",EDGE,"E47"),sQuery(id+"F16.wireOp",EDGE,"E64.2"),sQuery(id+"F16.wireOp",EDGE,"E67")])]})});
            var Q4;
            Q4=makeQuery(id+"F9.opExtrude","SWEPT_EDGE",EDGE,{"disambiguationData":[OSD([sQuery(id+"F0.wireOp",EDGE,"E0.left"),sQuery(id+"F8.wireOp",EDGE,"E47"),sQuery(id+"F8.wireOp",EDGE,"E48")])]});
            fillet(context, id + "F20", {"entities" : qUnion([Q0, Q1, Q2, Q3, Q4]), "radius" : 7 * mm, "tangentPropagation" : true, "allowEdgeOverflow" : false});
        }
    });
